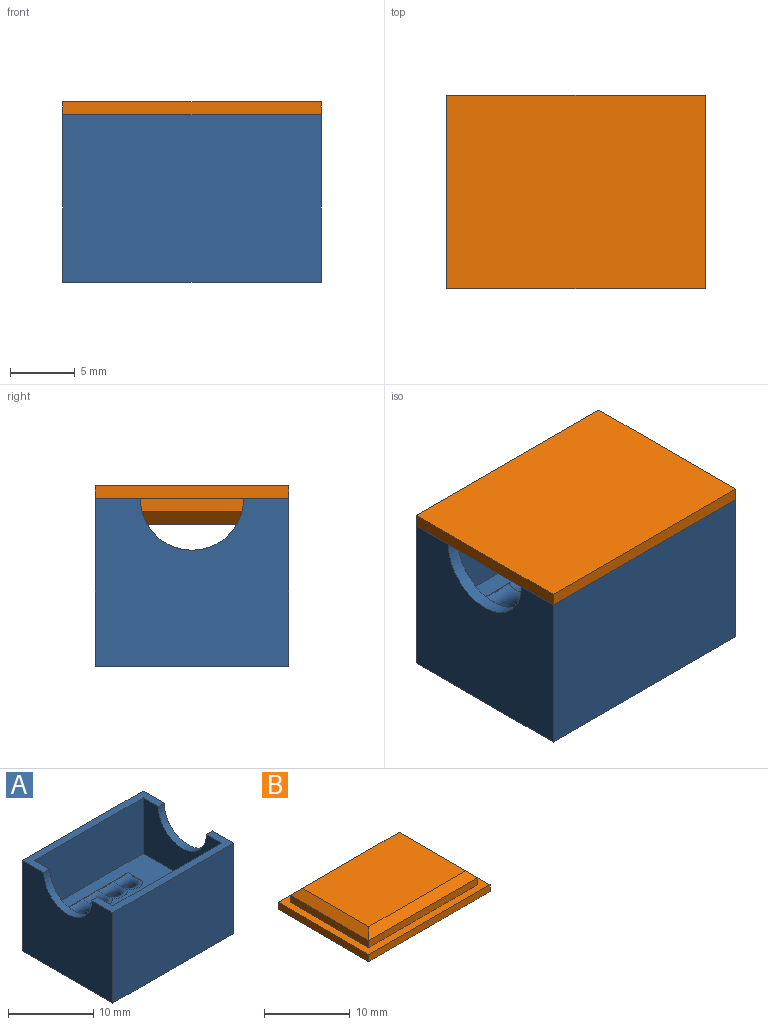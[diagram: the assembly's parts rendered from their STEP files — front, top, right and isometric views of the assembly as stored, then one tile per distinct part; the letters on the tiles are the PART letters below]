
ASSEMBLY  parts=2 mates=1
PART A: 42 faces, bbox 20x15x13 mm
  f0: plane 15x13mm, normal (-1,0,0), area 169.9mm2, adj f2,f20,f33,f34,f35,f41
  f1: plane 15x13mm, normal (1,0,0), area 169.9mm2, adj f2,f20,f33,f34,f35,f40
  f2: plane 20x3.5mm, normal (0,0,1), area 25mm2, adj f0,f1,f34,f36,f37,f39,f40,f41
  f3: plane 2.45x0.14mm, normal (0,-1,0), area 0.2mm2, adj f19,f21
  f4: plane 2.45x0.14mm, normal (0,-1,0), area 0.2mm2, adj f19,f22
  f5: plane 2.45x0.14mm, normal (0,-1,0), area 0.2mm2, adj f19,f23
  f6: plane 2.45x0.14mm, normal (1,0,0), area 0.2mm2, adj f19,f21
  f7: plane 2.45x0.14mm, normal (-1,0,0), area 0.2mm2, adj f19,f24
  f8: plane 2.45x0.14mm, normal (0,1,0), area 0.2mm2, adj f19,f25
  f9: plane 2.45x0.14mm, normal (0,1,0), area 0.2mm2, adj f19,f26
  f10: plane 2.45x0.14mm, normal (0,1,0), area 0.2mm2, adj f19,f27
  f11: cylinder r=0.75mm len=4mm, axis (0,0,-1), area 18.8mm2, adj f20,f21
  f12: cylinder r=0.75mm len=4mm, axis (0,0,-1), area 18.8mm2, adj f20,f22
  f13: cylinder r=0.75mm len=4mm, axis (0,0,-1), area 18.8mm2, adj f20,f23
  f14: cylinder r=0.75mm len=4mm, axis (0,0,-1), area 18.8mm2, adj f20,f25
  f15: cylinder r=0.75mm len=4mm, axis (0,0,-1), area 18.8mm2, adj f20,f26
  f16: cylinder r=0.75mm len=4mm, axis (0,0,-1), area 18.8mm2, adj f20,f27
  f17: cylinder r=0.75mm len=4mm, axis (0,0,-1), area 18.8mm2, adj f20,f28
  f18: cylinder r=0.75mm len=4mm, axis (0,0,-1), area 18.8mm2, adj f20,f24
  f19: plane 18x13mm, normal (0,0,1), area 177.3mm2, adj f3,f4,f5,f6,f7,f8,f9,f10
  f20: plane 20x15mm, normal (0,0,-1), area 285.9mm2, adj f0,f1,f11,f12,f13,f14,f15,f16
  f21: torus R=1.75mm, axis (0,0,1), area 8.4mm2, adj f3,f6,f11,f19,f22
  f22: torus R=1.75mm, axis (0,0,1), area 8.4mm2, adj f4,f12,f19,f21,f23
  f23: torus R=1.75mm, axis (0,0,1), area 8.4mm2, adj f5,f13,f19,f22,f24
  f24: torus R=1.75mm, axis (0,0,1), area 8.4mm2, adj f7,f18,f19,f23,f29
  f25: torus R=1.75mm, axis (0,0,1), area 8.4mm2, adj f8,f14,f19,f26,f30
  f26: torus R=1.75mm, axis (0,0,1), area 8.4mm2, adj f9,f15,f19,f25,f27
  f27: torus R=1.75mm, axis (0,0,1), area 8.4mm2, adj f10,f16,f19,f26,f28
  f28: torus R=1.75mm, axis (0,0,1), area 8.4mm2, adj f17,f19,f27,f31,f32
  f29: plane 2.45x0.14mm, normal (0,-1,0), area 0.2mm2, adj f19,f24
  f30: plane 2.45x0.14mm, normal (1,0,0), area 0.2mm2, adj f19,f25
  f31: plane 2.45x0.14mm, normal (-1,0,0), area 0.2mm2, adj f19,f28
  f32: plane 2.45x0.14mm, normal (0,1,0), area 0.2mm2, adj f19,f28
  f33: plane 20x13mm, normal (0,-1,0), area 260mm2, adj f0,f1,f20,f35
  f34: plane 20x13mm, normal (0,1,0), area 260mm2, adj f0,f1,f2,f20
  f35: plane 20x3.5mm, normal (0,0,1), area 25mm2, adj f0,f1,f33,f36,f38,f39,f40,f41
  f36: plane 13x8mm, normal (1,0,0), area 78.9mm2, adj f2,f19,f35,f37,f38,f41
  f37: plane 18x8mm, normal (0,-1,0), area 144mm2, adj f2,f19,f36,f39
  f38: plane 18x8mm, normal (0,1,0), area 144mm2, adj f19,f35,f36,f39
  f39: plane 13x8mm, normal (-1,0,0), area 78.9mm2, adj f2,f19,f35,f37,f38,f40
  f40: cylinder r=4mm len=8mm, axis (1,0,0), area 12.6mm2, adj f1,f2,f35,f39
  f41: cylinder r=4mm len=8mm, axis (1,0,0), area 12.6mm2, adj f0,f2,f35,f36
PART B: 15 faces, bbox 20x15x3 mm
  f0: plane 20x15mm, normal (0,0,1), area 66mm2, adj f1,f2,f3,f4,f6,f7,f8,f9
  f1: plane 20x1mm, normal (0,-1,0), area 20mm2, adj f0,f2,f4,f5
  f2: plane 15x1mm, normal (1,0,0), area 15mm2, adj f0,f1,f3,f5
  f3: plane 20x1mm, normal (0,1,0), area 20mm2, adj f0,f2,f4,f5
  f4: plane 15x1mm, normal (-1,0,0), area 15mm2, adj f0,f1,f3,f5
  f5: plane 20x15mm, normal (0,0,-1), area 300mm2, adj f1,f2,f3,f4
  f6: plane 13x1mm, normal (-1,0,0), area 13mm2, adj f0,f7,f9,f11
  f7: plane 18x1mm, normal (0,-1,0), area 18mm2, adj f0,f6,f8,f12
  f8: plane 13x1mm, normal (1,0,0), area 13mm2, adj f0,f7,f9,f14
  f9: plane 18x1mm, normal (0,1,0), area 18mm2, adj f0,f6,f8,f13
  f10: plane 16x11mm, normal (0,0,1), area 176mm2, adj f11,f12,f13,f14
  f11: plane 13x1mm, normal (-0.71,0,0.71), area 17mm2, adj f6,f10,f12,f13
  f12: plane 18x1mm, normal (0,-0.71,0.71), area 24mm2, adj f7,f10,f11,f14
  f13: plane 18x1mm, normal (0,0.71,0.71), area 24mm2, adj f9,f10,f11,f14
  f14: plane 13x1mm, normal (0.71,0,0.71), area 17mm2, adj f8,f10,f12,f13
PLACE A t=(-4.63,0.19,-7.87)mm
PLACE B rot(axis=(0,1,0),180deg) t=(-4.63,0.19,6.13)mm
MATE fastened B.f0 <-> A.f35  axis (0,0,-1) through (5.37,-7.31,5.13)mm
